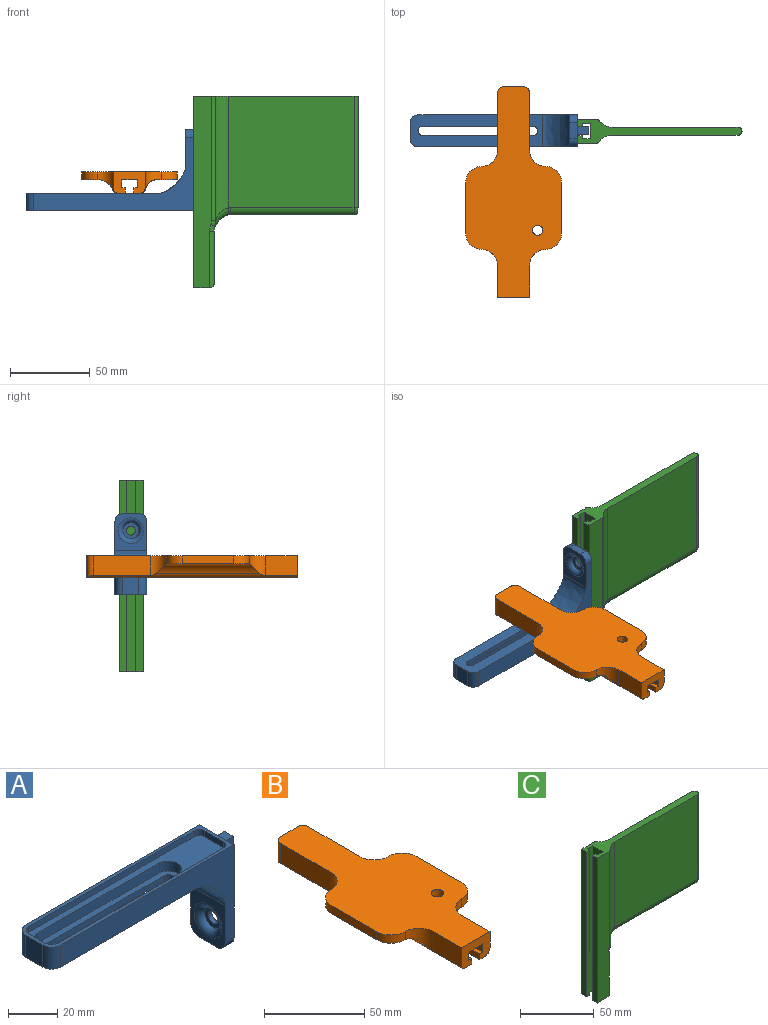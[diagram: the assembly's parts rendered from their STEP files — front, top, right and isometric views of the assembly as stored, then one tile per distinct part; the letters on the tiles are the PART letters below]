
ASSEMBLY  parts=3 mates=4
PART A: 39 faces, bbox 112x22x51.2 mm
  f0: plane 7x5mm, normal (0,0,1), area 35mm2, adj f8,f20,f22,f23
  f1: plane 102x17mm, normal (0,0,1), area 860.4mm2, adj f15,f16,f17,f18,f30,f31,f32,f33
  f2: cylinder r=2.75mm len=5.5mm, axis (-1,0,0), area 34.6mm2, adj f8,f24
  f3: cylinder r=2.76mm len=5.5mm, axis (0,0,-1), area 24.5mm2, adj f4,f6,f7,f19
  f4: plane 70x3mm, normal (0,1,0), area 210mm2, adj f3,f5,f7,f19
  f5: cylinder r=2.76mm len=5.5mm, axis (0,0,-1), area 24.5mm2, adj f4,f6,f7,f19
  f6: plane 70x3mm, normal (0,-1,0), area 210mm2, adj f3,f5,f7,f19
  f7: plane 83x20mm, normal (0,0,-1), area 1243.2mm2, adj f3,f4,f5,f6,f9,f10,f11,f14
  f8: plane 51x20mm, normal (1,0,0), area 935.5mm2, adj f0,f2,f9,f11,f13,f20,f21,f22
  f9: plane 100x46mm, normal (0,1,0), area 1357.1mm2, adj f7,f8,f12,f14,f26,f29,f38
  f10: plane 11x10mm, normal (-1,0,0), area 110mm2, adj f7,f28,f29,f38
  f11: plane 100x46mm, normal (0,-1,0), area 1357mm2, adj f7,f8,f12,f14,f27,f28,f38
  f12: plane 23x20mm, normal (-1,0,0), area 248.2mm2, adj f9,f11,f13,f14,f25,f26,f27
  f13: plane 10x5mm, normal (0,0,-1), area 50mm2, adj f8,f12,f26,f27
  f14: bspline ~22x17mm, area 514.5mm2, adj f7,f9,f11,f12
  f15: cylinder r=5.58mm len=11.1mm, axis (0,0,1), area 81.8mm2, adj f1,f16,f18,f19
  f16: plane 70x5mm, normal (0,1,0), area 350mm2, adj f1,f15,f17,f19
  f17: cylinder r=5.58mm len=11.1mm, axis (0,0,1), area 81.8mm2, adj f1,f16,f18,f19
  f18: plane 70x5mm, normal (0,-1,0), area 350mm2, adj f1,f15,f17,f19
  f19: plane 80x11.1mm, normal (0,0,1), area 455.8mm2, adj f3,f4,f5,f6,f15,f16,f17,f18
  f20: plane 10x7mm, normal (0,-1,0), area 70mm2, adj f0,f8,f21,f23
  f21: plane 7x5mm, normal (0,0,-1), area 35mm2, adj f8,f20,f22,f23
  f22: plane 10x7mm, normal (0,1,0), area 70mm2, adj f0,f8,f21,f23
  f23: plane 10x5mm, normal (1,0,0), area 50mm2, adj f0,f20,f21,f22
  f24: plane 10x10mm, normal (-1,0,0), area 54.8mm2, adj f2,f25
  f25: torus R=8mm, axis (1,0,0), area 180.3mm2, adj f12,f24
  f26: cylinder r=5mm len=5mm, axis (1,0,0), area 39.3mm2, adj f8,f9,f12,f13
  f27: cylinder r=5mm len=5mm, axis (-1,0,0), area 39.3mm2, adj f8,f11,f12,f13
  f28: cylinder r=5mm len=11mm, axis (0,0,1), area 86.4mm2, adj f7,f10,f11,f38
  f29: cylinder r=5mm len=11mm, axis (0,0,-1), area 86.4mm2, adj f7,f9,f10,f38
  f30: cylinder r=5mm len=3.5mm, axis (0,0,-1), area 15.4mm2, adj f1,f31,f37,f38
  f31: plane 10.04x3mm, normal (1,0,0), area 30.1mm2, adj f1,f30,f32,f38
  f32: cylinder r=5mm len=3.5mm, axis (0,0,-1), area 15.5mm2, adj f1,f31,f33,f38
  f33: plane 95.5x3mm, normal (0,-1,0), area 286.5mm2, adj f1,f32,f34,f38
  f34: cylinder r=3mm len=3mm, axis (0,0,-1), area 14.1mm2, adj f1,f33,f35,f38
  f35: plane 11x3mm, normal (-1,0,0), area 33mm2, adj f1,f34,f36,f38
  f36: cylinder r=3mm len=3mm, axis (0,0,-1), area 14.1mm2, adj f1,f35,f37,f38
  f37: plane 95.5x3mm, normal (0,1,0), area 286.5mm2, adj f1,f30,f36,f38
  f38: plane 105x20mm, normal (0,0,1), area 367mm2, adj f8,f9,f10,f11,f28,f29,f30,f31
PART B: 47 faces, bbox 61.9x133.9x15.4 mm
  f0: plane 20x12.16mm, normal (-1,0,0), area 243.2mm2, adj f12,f14,f30,f46
  f1: cylinder r=3.17mm len=6.35mm, axis (0,0,-1), area 99.7mm2, adj f7,f12
  f2: plane 132x3.54mm, normal (0,0,-1), area 419.9mm2, adj f13,f14,f21,f36,f37,f38,f39,f40
  f3: plane 20x9.5mm, normal (1,0,0), area 190mm2, adj f12,f14,f32,f43
  f4: plane 36x9.5mm, normal (1,0,0), area 342mm2, adj f12,f34,f35,f36
  f5: cylinder r=7mm len=39.7mm, axis (0,-1,0), area 307.2mm2, adj f7,f24,f34,f37,f38
  f6: cylinder r=7mm len=11.7mm, axis (0,-1,0), area 44.4mm2, adj f7,f25,f32,f42,f44
  f7: plane 54.81x24.39mm, normal (0,0,-1), area 748.7mm2, adj f1,f5,f6,f10,f23,f24,f25,f31
  f8: plane 52x10.11mm, normal (0,0,-1), area 483mm2, adj f11,f26,f27,f28,f29,f30
  f9: plane 132x9.8mm, normal (0,0,-1), area 1293.6mm2, adj f13,f14,f15,f16
  f10: plane 32x5mm, normal (1,0,0), area 160mm2, adj f7,f12,f31,f33
  f11: plane 32x5mm, normal (-1,0,0), area 160mm2, adj f8,f12,f26,f28
  f12: plane 132x60mm, normal (0,0,1), area 4681.5mm2, adj f0,f1,f3,f4,f10,f11,f13,f14
  f13: plane 13.5x12mm, normal (0,1,0), area 93.8mm2, adj f2,f9,f12,f15,f16,f17,f18,f19
  f14: plane 20x13.5mm, normal (0,-1,0), area 197.1mm2, adj f0,f2,f3,f9,f12,f15,f16,f17
  f15: plane 132x5mm, normal (-1,0,0), area 660mm2, adj f9,f13,f14,f20
  f16: plane 132x5mm, normal (1,0,0), area 660mm2, adj f9,f13,f14,f19
  f17: plane 132x3.5mm, normal (1,0,0), area 462mm2, adj f13,f14,f18,f19
  f18: plane 132x4.26mm, normal (0,0,-1), area 562.6mm2, adj f13,f14,f17,f45,f46
  f19: plane 132x2.15mm, normal (0,0,1), area 283.8mm2, adj f13,f14,f16,f17
  f20: plane 132x2.15mm, normal (0,0,1), area 283.8mm2, adj f13,f14,f15,f21
  f21: plane 132x3.5mm, normal (-1,0,0), area 462mm2, adj f2,f13,f14,f20
  f22: plane 36x12.16mm, normal (-1,0,0), area 437.8mm2, adj f12,f27,f45,f46
  f23: cylinder r=7.5mm len=11.77mm, axis (0,0,1), area 53.3mm2, adj f7,f24,f25,f40
  f24: bspline ~11.47x8.74mm, area 40.1mm2, adj f5,f7,f23,f39
  f25: bspline ~11.47x8.74mm, area 40.1mm2, adj f6,f7,f23,f41
  f26: cylinder r=10mm len=10mm, axis (0,0,1), area 78.5mm2, adj f8,f11,f12,f27
  f27: cylinder r=10mm len=12.16mm, axis (0,0,-1), area 129.6mm2, adj f8,f12,f22,f26,f29,f46
  f28: cylinder r=10mm len=10mm, axis (0,0,-1), area 78.5mm2, adj f8,f11,f12,f30
  f29: cylinder r=10mm len=64.7mm, axis (0,-1,0), area 681mm2, adj f8,f27,f30,f46
  f30: cylinder r=10mm len=12.16mm, axis (0,0,1), area 129.6mm2, adj f0,f8,f12,f28,f29,f46
  f31: cylinder r=10mm len=10mm, axis (0,0,1), area 78.5mm2, adj f7,f10,f12,f32
  f32: cylinder r=10mm len=10mm, axis (0,0,-1), area 113.9mm2, adj f3,f6,f7,f12,f31,f44
  f33: cylinder r=10mm len=10mm, axis (0,0,-1), area 78.5mm2, adj f7,f10,f12,f34
  f34: cylinder r=10mm len=10mm, axis (0,0,1), area 113.9mm2, adj f4,f5,f7,f12,f33,f37
  f35: cylinder r=4mm len=13.5mm, axis (0,0,1), area 72.3mm2, adj f4,f12,f13,f36
  f36: cylinder r=4mm len=40mm, axis (0,1,0), area 238.8mm2, adj f2,f4,f35,f37
  f37: torus R=14mm, axis (0,0,-1), area 16.3mm2, adj f2,f5,f34,f36,f38
  f38: cylinder r=4mm len=39.7mm, axis (0,-1,0), area 211.9mm2, adj f2,f5,f37,f39
  f39: bspline ~4.26x4.23mm, area 13.9mm2, adj f2,f24,f38,f40
  f40: torus R=11.5mm, axis (0,0,-1), area 76.3mm2, adj f2,f23,f39,f41
  f41: bspline ~4.72x4.29mm, area 13.9mm2, adj f2,f25,f40,f42
  f42: cylinder r=4mm len=11.7mm, axis (0,-1,0), area 61.7mm2, adj f2,f6,f41,f44
  f43: cylinder r=4mm len=20mm, axis (0,1,0), area 125.7mm2, adj f2,f3,f14,f44
  f44: torus R=14mm, axis (0,0,-1), area 16.3mm2, adj f2,f6,f32,f42,f43
  f45: cylinder r=4mm len=13.5mm, axis (0,0,-1), area 81.3mm2, adj f12,f13,f18,f22,f46
  f46: cylinder r=4mm len=131.87mm, axis (0,-1,0), area 526.8mm2, adj f0,f14,f18,f22,f27,f29,f30,f45
PART C: 37 faces, bbox 103x15x120 mm
  f0: plane 120x9.8mm, normal (-1,0,0), area 1176mm2, adj f3,f5,f8,f9
  f1: plane 78.84x70.06mm, normal (0,-1,0), area 5518.8mm2, adj f3,f18,f19,f20,f25
  f2: plane 78.84x70.06mm, normal (0,1,0), area 5518.8mm2, adj f3,f16,f21,f23,f25
  f3: plane 103x15mm, normal (0,0,1), area 601.3mm2, adj f0,f1,f2,f4,f6,f8,f9,f10
  f4: plane 120x11.41mm, normal (0,1,0), area 1314.4mm2, adj f3,f5,f14,f28,f29,f30,f31
  f5: plane 15x10mm, normal (0,0,-1), area 84.5mm2, adj f0,f4,f6,f8,f9,f10,f11,f12
  f6: plane 120x11.41mm, normal (0,-1,0), area 1314.4mm2, adj f3,f5,f12,f33,f34,f35,f36
  f7: plane 32x9mm, normal (1,0,0), area 288mm2, adj f17,f31,f32,f34
  f8: plane 120x5mm, normal (0,1,0), area 600mm2, adj f0,f3,f5,f10
  f9: plane 120x5mm, normal (0,-1,0), area 600mm2, adj f0,f3,f5,f15
  f10: plane 120x2.15mm, normal (1,0,0), area 258mm2, adj f3,f5,f8,f11
  f11: plane 120x3mm, normal (0,1,0), area 360mm2, adj f3,f5,f10,f12
  f12: plane 120x4.75mm, normal (-1,0,0), area 570mm2, adj f3,f5,f6,f11
  f13: plane 120x3mm, normal (0,-1,0), area 360mm2, adj f3,f5,f14,f15
  f14: plane 120x4.75mm, normal (-1,0,0), area 570mm2, adj f3,f4,f5,f13
  f15: plane 120x2.15mm, normal (1,0,0), area 258mm2, adj f3,f5,f9,f13
  f16: cylinder r=10mm len=77.81mm, axis (0,0,-1), area 671.3mm2, adj f2,f3,f24,f28
  f17: cylinder r=10mm len=9mm, axis (0,1,0), area 55.6mm2, adj f7,f22,f24,f30,f36
  f18: cylinder r=10mm len=77.81mm, axis (0,0,-1), area 671.3mm2, adj f1,f3,f22,f33
  f19: cylinder r=5mm len=77.5mm, axis (-1,0,0), area 405.8mm2, adj f1,f20,f21,f27
  f20: torus R=15mm, axis (0,-1,0), area 5.9mm2, adj f1,f19,f22,f23
  f21: cylinder r=5mm len=77.5mm, axis (1,0,0), area 405.8mm2, adj f2,f19,f23,f26
  f22: bspline ~11.89x10.79mm, area 64.5mm2, adj f17,f18,f20,f24,f35
  f23: torus R=15mm, axis (0,-1,0), area 5.9mm2, adj f2,f20,f21,f24
  f24: bspline ~11.89x10.79mm, area 64.5mm2, adj f16,f17,f22,f23,f29
  f25: cylinder r=2.5mm len=70mm, axis (0,0,1), area 549.8mm2, adj f1,f2,f3,f26,f27
  f26: torus R=2.5mm, axis (-1,0,0), area 9.3mm2, adj f21,f25,f27
  f27: torus R=2.5mm, axis (-1,0,0), area 9.3mm2, adj f19,f25,f26
  f28: cylinder r=3mm len=77.81mm, axis (0,0,-1), area 211.9mm2, adj f3,f4,f16,f29
  f29: bspline ~4.74x3.49mm, area 12mm2, adj f4,f24,f28,f30
  f30: torus R=13mm, axis (0,1,0), area 18.9mm2, adj f4,f17,f29,f31
  f31: cylinder r=3mm len=35mm, axis (0,0,1), area 157.9mm2, adj f4,f7,f30,f32
  f32: cylinder r=3mm len=15mm, axis (0,1,0), area 56.5mm2, adj f5,f7,f31,f34
  f33: cylinder r=3mm len=77.81mm, axis (0,0,-1), area 211.9mm2, adj f3,f6,f18,f35
  f34: cylinder r=3mm len=35mm, axis (0,0,-1), area 157.9mm2, adj f6,f7,f32,f36
  f35: bspline ~4.74x3.49mm, area 12mm2, adj f6,f22,f33,f36
  f36: torus R=13mm, axis (0,1,0), area 18.9mm2, adj f6,f17,f34,f35
PLACE A rot(axis=(1,0,0),180deg) t=(-12.71,40.7,-38.89)mm
PLACE B t=(-0.3,-7.58,-30.39)mm
PLACE C t=(92.45,42.95,-15.55)mm fixed
MATE planar A.f20 <-> C.f13  axis (0,1,0) through (39.79,43.2,-41.89)mm
MATE planar B.f2 <-> A.f7  axis (0,0,-1) through (4.1,3.6,-38.89)mm
MATE parallel B.f8 <-> A.f7  axis (0,0,-1) through (-24.99,-7.58,-30.39)mm
MATE planar A.f8 <-> C.f14  axis (1,0,0) through (39.79,43.2,-46.89)mm
